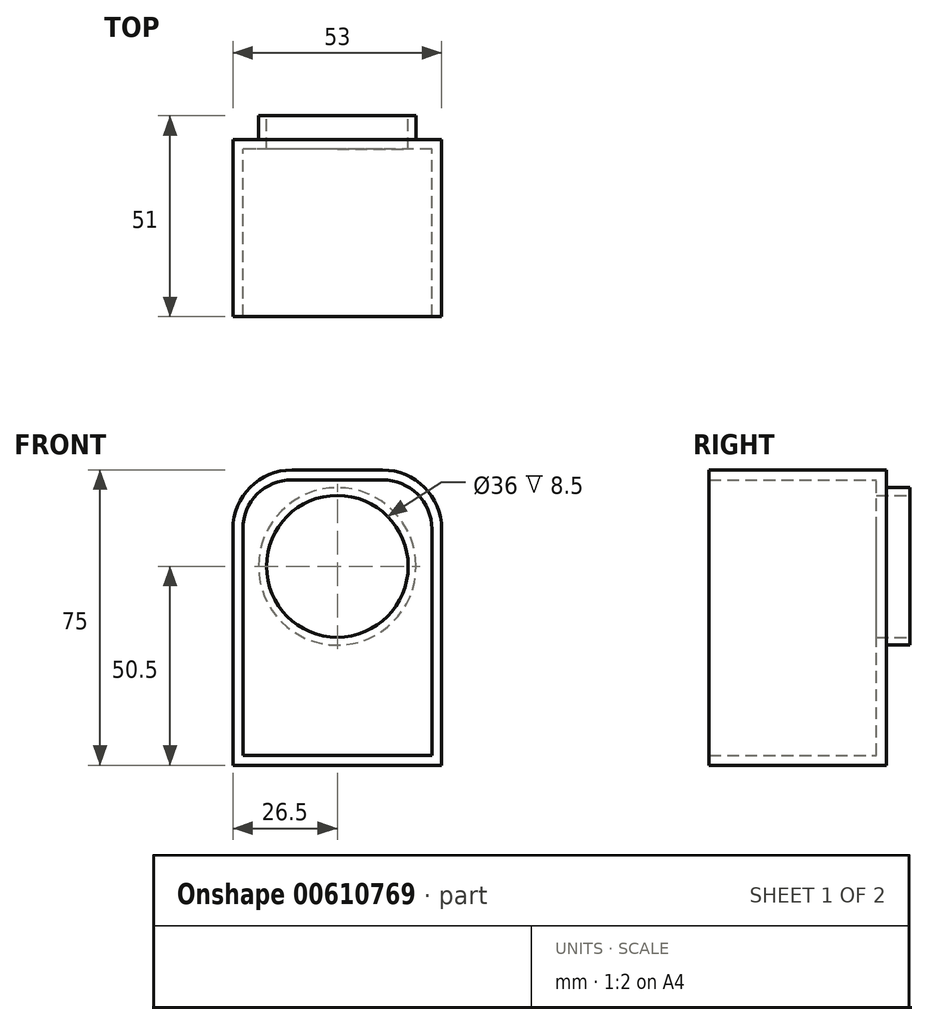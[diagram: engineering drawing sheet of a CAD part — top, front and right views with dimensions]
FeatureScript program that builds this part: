
annotation { "Feature Type Name" : "Feature", "Feature Type Description" : "" }
export const myFeature = defineFeature(function(context is Context, id is Id, definition is map)
    precondition{}
    {
        {
            var Q0;
            Q0=qCreatedBy(makeId("Front.planeOp"),FACE);
            var sketch = newSketch(context, id + "F0", { "sketchPlane" : qUnion([Q0])});
            skLineSegment(sketch, "E0.bottom", {"start": v(26.5, -37.5) * mm, "end": v(-26.5, -37.5) * mm});
            skLineSegment(sketch, "E0.top", {"start": v(11.5, 37.5) * mm, "end": v(-11.5, 37.5) * mm});
            skLineSegment(sketch, "E0.left", {"start": v(26.5, -37.5) * mm, "end": v(26.5, 22.5) * mm});
            skLineSegment(sketch, "E0.right", {"start": v(-26.5, -37.5) * mm, "end": v(-26.5, 22.5) * mm});
            skPoint(sketch, "E0.middle", {"position": v(0, 0) * mm});
            skPoint(sketch, "E1.center.orphan", {"position": v(0, 37.5) * mm});
            skPoint(sketch, "E2.visualSharp", {"position": v(-26.5, 37.5) * mm});
            skArc(sketch, "E2.filletArc", {"start": v(-11.5, 37.5) * mm, "mid": v(-22.1, 33.1) * mm, "end": v(-26.5, 22.5) * mm});
            skPoint(sketch, "E3.visualSharp", {"position": v(26.5, 37.5) * mm});
            skArc(sketch, "E3.filletArc", {"start": v(26.5, 22.5) * mm, "mid": v(22.1, 33.1) * mm, "end": v(11.5, 37.5) * mm});
            skSolve(sketch);
        }
        {
            var Q0;
            Q0=makeQuery(id+"F0.imprint","IMPRINT",FACE,{"disambiguationData":[TD([[makeQuery(id+"F0.imprint","IMPRINT",EDGE,{"derivedFrom":sQuery(id+"F0.wireOp",EDGE,"E0.bottom")}),-1.0]])]});
            extrude(context, id + "F1", {"entities" : qUnion([Q0]), "depth" : 45 * mm, "offsetDistance" : 25 * mm});
        }
        {
            var Q0;
            Q0=makeQuery(id+"F1.opExtrude","CAP_FACE",FACE,{"disambiguationData":[OSD([sQuery(id+"F0.wireOp",EDGE,"E0.bottom"),sQuery(id+"F0.wireOp",EDGE,"E0.top"),sQuery(id+"F0.wireOp",EDGE,"E0.left"),sQuery(id+"F0.wireOp",EDGE,"E0.right"),sQuery(id+"F0.wireOp",EDGE,"E2.filletArc"),sQuery(id+"F0.wireOp",EDGE,"E3.filletArc")])],"isStart":false});
            shell(context, id + "F2", {"entities" : qUnion([Q0]), "thickness" : 2.5 * mm});
        }
        {
            var Q0;
            Q0=makeQuery(id+"F1.opExtrude","CAP_FACE",FACE,{"disambiguationData":[OSD([sQuery(id+"F0.wireOp",EDGE,"E0.bottom"),sQuery(id+"F0.wireOp",EDGE,"E0.top"),sQuery(id+"F0.wireOp",EDGE,"E0.left"),sQuery(id+"F0.wireOp",EDGE,"E0.right"),sQuery(id+"F0.wireOp",EDGE,"E2.filletArc"),sQuery(id+"F0.wireOp",EDGE,"E3.filletArc")])],"isStart":true});
            var sketch = newSketch(context, id + "F3", { "sketchPlane" : qUnion([Q0])});
            skCircle(sketch, "E4", {"center": v(0, 13) * mm, "radius": 18 * mm});
            skSolve(sketch);
        }
        {
            var Q0;
            Q0=makeQuery(id+"F3.imprint","IMPRINT",FACE,{"disambiguationData":[TD([[makeQuery(id+"F3.imprint","IMPRINT",EDGE,{"derivedFrom":sQuery(id+"F3.wireOp",EDGE,"E4")}),1.0]])]});
            extrude(context, id + "F4", {"entities" : qUnion([Q0]), "operationType" : NewBodyOperationType.REMOVE, "oppositeDirection" : true, "depth" : 25 * mm, "offsetDistance" : 25 * mm});
        }
        {
            var Q0;
            Q0=makeQuery(id+"F1.opExtrude","CAP_FACE",FACE,{"disambiguationData":[OSD([sQuery(id+"F0.wireOp",EDGE,"E0.bottom"),sQuery(id+"F0.wireOp",EDGE,"E0.top"),sQuery(id+"F0.wireOp",EDGE,"E0.left"),sQuery(id+"F0.wireOp",EDGE,"E0.right"),sQuery(id+"F0.wireOp",EDGE,"E2.filletArc"),sQuery(id+"F0.wireOp",EDGE,"E3.filletArc")])],"isStart":true});
            var sketch = newSketch(context, id + "F5", { "sketchPlane" : qUnion([Q0])});
            skCircle(sketch, "E5.0", {"center": v(0, 13) * mm, "radius": 18 * mm});
            skCircle(sketch, "E6.0", {"center": v(0, 13) * mm, "radius": 20 * mm});
            skSolve(sketch);
        }
        {
            var Q0;
            Q0=makeQuery(id+"F5.imprint","IMPRINT",FACE,{"disambiguationData":[TD([[makeQuery(id+"F5.imprint","IMPRINT",EDGE,{"derivedFrom":sQuery(id+"F5.wireOp",EDGE,"E5.0")}),-1.0]])]});
            extrude(context, id + "F6", {"entities" : qUnion([Q0]), "operationType" : NewBodyOperationType.ADD, "depth" : 6 * mm, "offsetDistance" : 25 * mm});
        }
    });
